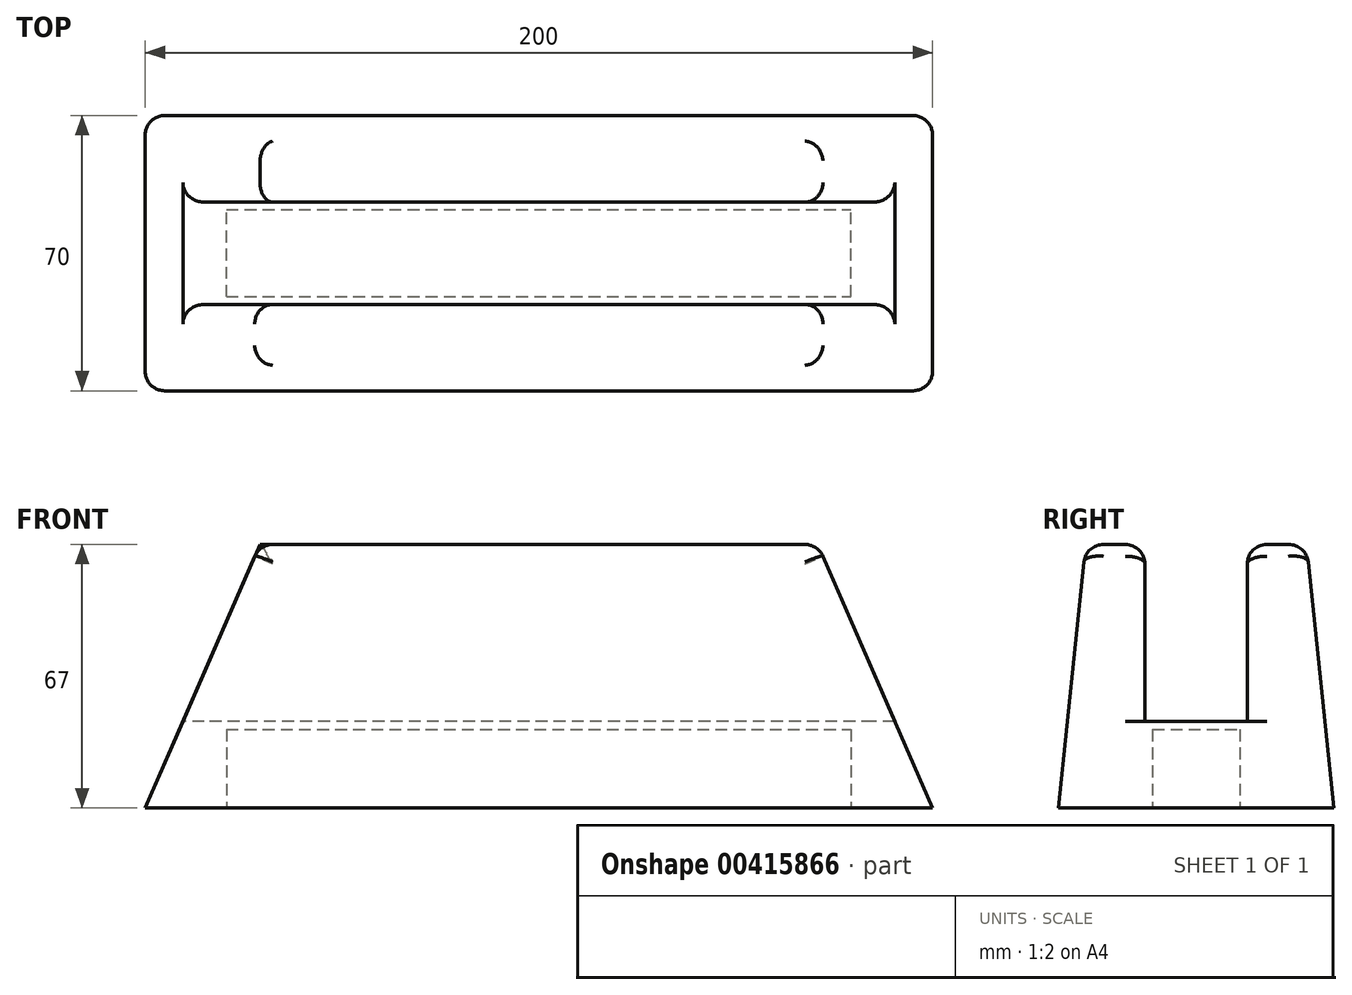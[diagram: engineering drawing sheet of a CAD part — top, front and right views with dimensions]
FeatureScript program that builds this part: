
annotation { "Feature Type Name" : "Feature", "Feature Type Description" : "" }
export const myFeature = defineFeature(function(context is Context, id is Id, definition is map)
    precondition{}
    {
        {
            var Q0;
            Q0=qCreatedBy(makeId("Right.planeOp"),FACE);
            var sketch = newSketch(context, id + "F0", { "sketchPlane" : qUnion([Q0])});
            skLineSegment(sketch, "E0.bottom", {"start": v(-35, 11) * mm, "end": v(35, 11) * mm});
            skLineSegment(sketch, "E0.top", {"start": v(-35, -11) * mm, "end": v(35, -11) * mm});
            skLineSegment(sketch, "E0.left", {"start": v(-35, 10.66) * mm, "end": v(-35, -11) * mm});
            skLineSegment(sketch, "E0.right", {"start": v(35, 10.66) * mm, "end": v(35, -11) * mm});
            skPoint(sketch, "E0.middle", {"position": v(0, 0) * mm});
            skLineSegment(sketch, "E1", {"start": v(0, 11) * mm, "end": v(0, 86) * mm, "construction": true});
            skPoint(sketch, "E1.endSnap0", {"position": v(0, 11) * mm});
            skLineSegment(sketch, "E2.bottom", {"start": v(12.98, 11) * mm, "end": v(-13.02, 11) * mm});
            skLineSegment(sketch, "E2.top", {"start": v(13.02, 161) * mm, "end": v(-12.98, 161) * mm});
            skPoint(sketch, "E2.middle", {"position": v(0, 86) * mm});
            skPoint(sketch, "E3.visualSharp", {"position": v(-12.98, 161) * mm});
            skPoint(sketch, "E4.visualSharp", {"position": v(13.02, 161) * mm});
            skPoint(sketch, "E5.visualSharp", {"position": v(-35, 11) * mm});
            skArc(sketch, "E5.filletArc", {"start": v(-34.89, 11.32) * mm, "mid": v(-34.97, 11) * mm, "end": v(-35, 10.66) * mm});
            skPoint(sketch, "E6.visualSharp", {"position": v(35, 11) * mm});
            skArc(sketch, "E6.filletArc", {"start": v(35, 10.66) * mm, "mid": v(34.97, 11) * mm, "end": v(34.89, 11.32) * mm});
            skLineSegment(sketch, "E7", {"start": v(-13.02, 11) * mm, "end": v(-13.02, 56) * mm});
            skLineSegment(sketch, "E8", {"start": v(12.98, 11) * mm, "end": v(12.98, 56) * mm});
            skLineSegment(sketch, "E9", {"start": v(-13.02, 56) * mm, "end": v(-28.02, 56) * mm});
            skLineSegment(sketch, "E10", {"start": v(12.98, 56) * mm, "end": v(27.98, 56) * mm});
            skLineSegment(sketch, "E11", {"start": v(-28.02, 56) * mm, "end": v(-35, -11) * mm});
            skLineSegment(sketch, "E12", {"start": v(27.98, 56) * mm, "end": v(35, -11) * mm});
            skSolve(sketch);
        }
        {
            var Q0;
            {var subQ2=sQuery(id+"F0.wireOp",EDGE,"E2.right");Q0=makeQuery(id+"F0.imprint","IMPRINT",FACE,{"disambiguationData":[TD([[makeQuery(id+"F0.imprint","IMPRINT",EDGE,{"derivedFrom":subQ2}),1.0]])]});}
            var Q1;
            Q1=makeQuery(id+"F0.imprint","IMPRINT",FACE,{"disambiguationData":[TD([[makeQuery(id+"F0.imprint","IMPRINT",EDGE,{"derivedFrom":sQuery(id+"F0.wireOp",EDGE,"E0.top")}),1.0]])]});
            var Q2;
            {var subQ2=sQuery(id+"F0.wireOp",EDGE,"E2.left");Q2=makeQuery(id+"F0.imprint","IMPRINT",FACE,{"disambiguationData":[TD([[makeQuery(id+"F0.imprint","IMPRINT",EDGE,{"derivedFrom":subQ2}),-1.0]])]});}
            var Q3;
            {var subQ0=sQuery(id+"F0.wireOp",EDGE,"wDXZBjZO-bxPW-lPxb-0Ool-IlhOLcgPC1Tl");Q3=makeQuery(id+"F0.imprint","IMPRINT",FACE,{"disambiguationData":[TD([[makeQuery(id+"F0.imprint","IMPRINT",EDGE,{"derivedFrom":subQ0}),-1.0]])]});}
            var Q4;
            {var subQ0=sQuery(id+"F0.wireOp",EDGE,"DRrN5l3Y-3Tt4-BfDu-wpdq-V9KRQ8uc1MHb");Q4=makeQuery(id+"F0.imprint","IMPRINT",FACE,{"disambiguationData":[TD([[makeQuery(id+"F0.imprint","IMPRINT",EDGE,{"derivedFrom":subQ0}),1.0]])]});}
            var Q5;
            {var subQ0=sQuery(id+"F0.wireOp",EDGE,"E8");Q5=makeQuery(id+"F0.imprint","IMPRINT",FACE,{"disambiguationData":[TD([[makeQuery(id+"F0.imprint","IMPRINT",EDGE,{"derivedFrom":subQ0}),-1.0]])]});}
            var Q6;
            {var subQ0=sQuery(id+"F0.wireOp",EDGE,"E7");Q6=makeQuery(id+"F0.imprint","IMPRINT",FACE,{"disambiguationData":[TD([[makeQuery(id+"F0.imprint","IMPRINT",EDGE,{"derivedFrom":subQ0}),1.0]])]});}
            extrude(context, id + "F1", {"entities" : qUnion([Q0, Q1, Q2, Q3, Q4, Q5, Q6]), "depth" : 200 * mm});
        }
        {
            var Q0;
            Q0=makeQuery(id+"F1.opExtrude","SWEPT_FACE",FACE,{"disambiguationData":[OSD([sQuery(id+"F0.wireOp",EDGE,"E0.top")])]});
            var sketch = newSketch(context, id + "F2", { "sketchPlane" : qUnion([Q0])});
            skLineSegment(sketch, "E13.bottom", {"start": v(20.67, 11.07) * mm, "end": v(179.33, 11.07) * mm});
            skLineSegment(sketch, "E13.top", {"start": v(20.67, -11.07) * mm, "end": v(179.33, -11.07) * mm});
            skLineSegment(sketch, "E13.left", {"start": v(20.67, 11.07) * mm, "end": v(20.67, -11.07) * mm});
            skLineSegment(sketch, "E13.right", {"start": v(179.33, 11.07) * mm, "end": v(179.33, -11.07) * mm});
            skPoint(sketch, "E13.middle", {"position": v(100, 0) * mm});
            skPoint(sketch, "E13.middle.positionSnap0", {"position": v(100, 35) * mm});
            skPoint(sketch, "E13.centerSnap0", {"position": v(100, 35) * mm});
            skSolve(sketch);
        }
        {
            var Q0;
            Q0=makeQuery(id+"F2.imprint","IMPRINT",FACE,{"disambiguationData":[TD([[makeQuery(id+"F2.imprint","IMPRINT",EDGE,{"derivedFrom":sQuery(id+"F2.wireOp",EDGE,"E13.bottom")}),-1.0]])]});
            extrude(context, id + "F3", {"entities" : qUnion([Q0]), "operationType" : NewBodyOperationType.REMOVE, "oppositeDirection" : true, "depth" : 20 * mm});
        }
        {
            var Q0;
            Q0=qCreatedBy(makeId("Front.planeOp"),FACE);
            var sketch = newSketch(context, id + "F4", { "sketchPlane" : qUnion([Q0])});
            skLineSegment(sketch, "E14.0", {"start": v(200, 56) * mm, "end": v(0, 56) * mm});
            skLineSegment(sketch, "E15.0", {"start": v(200, -11) * mm, "end": v(0, -11) * mm});
            skLineSegment(sketch, "E16.0", {"start": v(0, 56) * mm, "end": v(0, -11) * mm});
            skLineSegment(sketch, "E17.0", {"start": v(200, 56) * mm, "end": v(200, -11) * mm});
            skLineSegment(sketch, "E18", {"start": v(0, -11) * mm, "end": v(29.13, 56) * mm});
            skLineSegment(sketch, "E19", {"start": v(200, -11) * mm, "end": v(170.87, 56) * mm});
            skSolve(sketch);
        }
        {
            var Q0;
            {var subQ0=sQuery(id+"F4.wireOp",EDGE,"E16.0");Q0=makeQuery(id+"F4.imprint","IMPRINT",FACE,{"disambiguationData":[TD([[makeQuery(id+"F4.imprint","IMPRINT",EDGE,{"derivedFrom":subQ0}),1.0]])]});}
            var Q1;
            {var subQ0=sQuery(id+"F4.wireOp",EDGE,"E17.0");Q1=makeQuery(id+"F4.imprint","IMPRINT",FACE,{"disambiguationData":[TD([[makeQuery(id+"F4.imprint","IMPRINT",EDGE,{"derivedFrom":subQ0}),-1.0]])]});}
            extrude(context, id + "F5", {"entities" : qUnion([Q0, Q1]), "operationType" : NewBodyOperationType.REMOVE, "endBound" : BoundingType.SYMMETRIC, "oppositeDirection" : true, "depth" : 150 * mm});
        }
        {
            var Q0;
            Q0=makeQuery(id+"F1.opExtrude","SWEPT_EDGE",EDGE,{"disambiguationData":[OSD([sQuery(id+"F0.wireOp",EDGE,"E9"),sQuery(id+"F0.wireOp",EDGE,"E11")])]});
            var Q1;
            Q1=makeQuery(id+"F1.opExtrude","SWEPT_EDGE",EDGE,{"disambiguationData":[OSD([sQuery(id+"F0.wireOp",EDGE,"E7"),sQuery(id+"F0.wireOp",EDGE,"E9")])]});
            var Q2;
            Q2=makeQuery(id+"F1.opExtrude","SWEPT_EDGE",EDGE,{"disambiguationData":[OSD([sQuery(id+"F0.wireOp",EDGE,"E8"),sQuery(id+"F0.wireOp",EDGE,"E10")])]});
            var Q3;
            Q3=makeQuery(id+"F1.opExtrude","SWEPT_EDGE",EDGE,{"disambiguationData":[OSD([sQuery(id+"F0.wireOp",EDGE,"E10"),sQuery(id+"F0.wireOp",EDGE,"E12")])]});
            var Q4;
            Q4=makeQuery(id+"F5.boolean.opBoolean","INTERSECT",EDGE,{"derivedFrom":[makeQuery(id+"F1.opExtrude","SWEPT_FACE",FACE,{"disambiguationData":[OSD([sQuery(id+"F0.wireOp",EDGE,"E8")])]}),makeQuery(id+"F5.opExtrude","SWEPT_FACE",FACE,{"disambiguationData":[OSD([sQuery(id+"F4.wireOp",EDGE,"E19")])]})]});
            var Q5;
            Q5=makeQuery(id+"F5.boolean.opBoolean","INTERSECT",EDGE,{"derivedFrom":[makeQuery(id+"F1.opExtrude","SWEPT_FACE",FACE,{"disambiguationData":[OSD([sQuery(id+"F0.wireOp",EDGE,"E11")])]}),makeQuery(id+"F5.opExtrude","SWEPT_FACE",FACE,{"disambiguationData":[OSD([sQuery(id+"F4.wireOp",EDGE,"E19")])]})]});
            var Q6;
            Q6=makeQuery(id+"F5.boolean.opBoolean","INTERSECT",EDGE,{"derivedFrom":[makeQuery(id+"F1.opExtrude","SWEPT_FACE",FACE,{"disambiguationData":[OSD([sQuery(id+"F0.wireOp",EDGE,"E7")])]}),makeQuery(id+"F5.opExtrude","SWEPT_FACE",FACE,{"disambiguationData":[OSD([sQuery(id+"F4.wireOp",EDGE,"E19")])]})]});
            var Q7;
            Q7=makeQuery(id+"F5.boolean.opBoolean","INTERSECT",EDGE,{"derivedFrom":[makeQuery(id+"F1.opExtrude","SWEPT_FACE",FACE,{"disambiguationData":[OSD([sQuery(id+"F0.wireOp",EDGE,"E2.bottom")])]}),makeQuery(id+"F5.opExtrude","SWEPT_FACE",FACE,{"disambiguationData":[OSD([sQuery(id+"F4.wireOp",EDGE,"E19")])]})]});
            var Q8;
            Q8=makeQuery(id+"F5.boolean.opBoolean","INTERSECT",EDGE,{"derivedFrom":[makeQuery(id+"F1.opExtrude","SWEPT_FACE",FACE,{"disambiguationData":[OSD([sQuery(id+"F0.wireOp",EDGE,"E12")])]}),makeQuery(id+"F5.opExtrude","SWEPT_FACE",FACE,{"disambiguationData":[OSD([sQuery(id+"F4.wireOp",EDGE,"E19")])]})]});
            var Q9;
            Q9=makeQuery(id+"F5.boolean.opBoolean","INTERSECT",EDGE,{"derivedFrom":[makeQuery(id+"F1.opExtrude","SWEPT_FACE",FACE,{"disambiguationData":[OSD([sQuery(id+"F0.wireOp",EDGE,"E11")])]}),makeQuery(id+"F5.opExtrude","SWEPT_FACE",FACE,{"disambiguationData":[OSD([sQuery(id+"F4.wireOp",EDGE,"E18")])]})]});
            var Q10;
            Q10=makeQuery(id+"F5.boolean.opBoolean","INTERSECT",EDGE,{"derivedFrom":[makeQuery(id+"F1.opExtrude","SWEPT_FACE",FACE,{"disambiguationData":[OSD([sQuery(id+"F0.wireOp",EDGE,"E7")])]}),makeQuery(id+"F5.opExtrude","SWEPT_FACE",FACE,{"disambiguationData":[OSD([sQuery(id+"F4.wireOp",EDGE,"E18")])]})]});
            var Q11;
            Q11=makeQuery(id+"F5.boolean.opBoolean","INTERSECT",EDGE,{"derivedFrom":[makeQuery(id+"F1.opExtrude","SWEPT_FACE",FACE,{"disambiguationData":[OSD([sQuery(id+"F0.wireOp",EDGE,"E2.bottom")])]}),makeQuery(id+"F5.opExtrude","SWEPT_FACE",FACE,{"disambiguationData":[OSD([sQuery(id+"F4.wireOp",EDGE,"E18")])]})]});
            var Q12;
            Q12=makeQuery(id+"F5.boolean.opBoolean","INTERSECT",EDGE,{"derivedFrom":[makeQuery(id+"F1.opExtrude","SWEPT_FACE",FACE,{"disambiguationData":[OSD([sQuery(id+"F0.wireOp",EDGE,"E8")])]}),makeQuery(id+"F5.opExtrude","SWEPT_FACE",FACE,{"disambiguationData":[OSD([sQuery(id+"F4.wireOp",EDGE,"E18")])]})]});
            var Q13;
            Q13=makeQuery(id+"F5.boolean.opBoolean","INTERSECT",EDGE,{"derivedFrom":[makeQuery(id+"F1.opExtrude","SWEPT_FACE",FACE,{"disambiguationData":[OSD([sQuery(id+"F0.wireOp",EDGE,"E12")])]}),makeQuery(id+"F5.opExtrude","SWEPT_FACE",FACE,{"disambiguationData":[OSD([sQuery(id+"F4.wireOp",EDGE,"E18")])]})]});
            fillet(context, id + "F6", {"entities" : qUnion([Q0, Q1, Q2, Q3, Q4, Q5, Q6, Q7, Q8, Q9, Q10, Q11, Q12, Q13]), "radius" : 5 * mm, "tangentPropagation" : true, "allowEdgeOverflow" : false});
        }
        {
            var Q0;
            {var subQ0=sQuery(id+"F4.wireOp",EDGE,"E18");Q0=makeQuery(id+"F5.boolean.opBoolean","COPY",EDGE,{"disambiguationData":[topologyDisambiguationEdgeConnected([makeQuery(id+"F1.opExtrude","SWEPT_FACE",FACE,{"disambiguationData":[OSD([sQuery(id+"F0.wireOp",EDGE,"E10")])]})])],"derivedFrom":makeQuery(id+"F5.opExtrude","SWEPT_EDGE",EDGE,{"disambiguationData":[OSD([sQuery(id+"F4.wireOp",EDGE,"E14.0"),subQ0])]})});}
            var Q1;
            {var subQ0=sQuery(id+"F0.wireOp",EDGE,"E11");Q1=makeQuery(id+"F6.opFillet","BLEND_EDGE",EDGE,{"blendedFrom":[makeQuery(id+"F1.opExtrude","SWEPT_EDGE",EDGE,{"disambiguationData":[OSD([sQuery(id+"F0.wireOp",EDGE,"E9"),subQ0])]}),makeQuery(id+"F5.boolean.opBoolean","INTERSECT",EDGE,{"derivedFrom":[makeQuery(id+"F1.opExtrude","SWEPT_FACE",FACE,{"disambiguationData":[OSD([subQ0])]}),makeQuery(id+"F5.opExtrude","SWEPT_FACE",FACE,{"disambiguationData":[OSD([sQuery(id+"F4.wireOp",EDGE,"E18")])]})]})],"blendedInto":[]});}
            var Q2;
            {var subQ0=sQuery(id+"F0.wireOp",EDGE,"E7");Q2=makeQuery(id+"F6.opFillet","BLEND_EDGE",EDGE,{"blendedFrom":[makeQuery(id+"F1.opExtrude","SWEPT_EDGE",EDGE,{"disambiguationData":[OSD([subQ0,sQuery(id+"F0.wireOp",EDGE,"E9")])]}),makeQuery(id+"F5.boolean.opBoolean","INTERSECT",EDGE,{"derivedFrom":[makeQuery(id+"F1.opExtrude","SWEPT_FACE",FACE,{"disambiguationData":[OSD([subQ0])]}),makeQuery(id+"F5.opExtrude","SWEPT_FACE",FACE,{"disambiguationData":[OSD([sQuery(id+"F4.wireOp",EDGE,"E19")])]})]})],"blendedInto":[]});}
            var Q3;
            {var subQ0=sQuery(id+"F0.wireOp",EDGE,"E12");Q3=makeQuery(id+"F6.opFillet","BLEND_EDGE",EDGE,{"blendedFrom":[makeQuery(id+"F1.opExtrude","SWEPT_EDGE",EDGE,{"disambiguationData":[OSD([sQuery(id+"F0.wireOp",EDGE,"E10"),subQ0])]}),makeQuery(id+"F5.boolean.opBoolean","INTERSECT",EDGE,{"derivedFrom":[makeQuery(id+"F1.opExtrude","SWEPT_FACE",FACE,{"disambiguationData":[OSD([subQ0])]}),makeQuery(id+"F5.opExtrude","SWEPT_FACE",FACE,{"disambiguationData":[OSD([sQuery(id+"F4.wireOp",EDGE,"E19")])]})]})],"blendedInto":[]});}
            fillet(context, id + "F7", {"entities" : qUnion([Q0, Q1, Q2, Q3]), "radius" : 5 * mm, "tangentPropagation" : true, "allowEdgeOverflow" : false});
        }
    });
